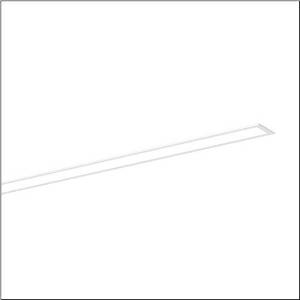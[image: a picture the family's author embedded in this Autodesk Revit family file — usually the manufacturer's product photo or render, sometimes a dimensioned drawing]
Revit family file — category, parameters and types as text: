
# Revit family: silica_21_51mx10db42wb
name_source: partatom
category: Lighting Fixtures
units: mm (PartAtom-declared; Revit-internal decimal feet)

## family parameters
Cut with Voids When Loaded = No
Host = Face
Light Source = No
Part Type = Normal
Room Calculation Point = No
Round Connector Dimension = Use Diameter
Shared = No

## types (1)
- --- (1 x LED, 3000 lm, 19 W, 4000K)
    Apparent Load = 19 VA
    CIE Flux Codes = 48 79 96 100 100
    Color Rendering = 80
    Color Temperature = 4000K
    Default Elevation = 1800 mm
    Description = Silica 21, office luminaire, primary optical cover: cover, of PMMA, opal, light emission: direct distribution, primary light characteristic: symmetric, installation type: recessed, LED, rated luminous flux: 3.000lm, luminous efficacy: 158lm/W, light colour: 840, colour temperature: 4000K, control gear: DALI 2, with terminal, 3+2-pole, max. 2.5mm², mains connection: 220..240V, AC, 50/60Hz, rated input power: 19W, luminaire housing, of aluminium, traffic white (RAL 9016), length: 1.528mm, width: 79mm, height: 53mm, protection rating (complete): IP20, insulation class (complete): insulation class I (protective earthing), certification: CE, ENEC, VDE, permissible operating ambient temperature: 0..+35°C, standard: EN 50419, packaging unit: 1 piece
    Height = 0 mm  [stored 0 ft]
    Lamp = 1 x LED
    Lamp Light Flux = 3000 lm
    Lamp Power = 19 W
    Lamp count = 1
    Length = 1527 mm
    Luminous efficacy = 158 lm/W
    Manufacturer = Siteco
    ModVariant = No
    Model = 51MX10DB42WB
    Mounting Place = Ceiling
    Mounting Type = Recessed
    Number of Poles = 1
    OnlyDefault = Yes
    Power Factor = 1
    Product Name = Silica 21
    Product group = office luminaire | ceiling recessed
    ProductGroupID = 400
    Protection Class = Protection class I
    Protection Degree = IP 20
    RLX_Detail_Level = 1
    RLX_Emergency_Light_Flux = 0 lm
    RLX_Emergency_Type = 0
    RLX_Emergency_Type_DB = No
    RlxData = <blob elided: 21033 chars, md5=160e235e>
    Socket = socket
    Standby Power = 0 W
    System Light Flux = 3000 lm
    System Power = 19 W
    Type Comments = factory setting: luminous flux: 100 % | dim-lin: 254 | 218 mA
    Type Image = l_1335891.jpg
    URL = http://relux.com
    VarID = @adj_117845
    Voltage = 0 V
    Weight = 0.00 kg
    Width = 79 mm

note: [stored X ft] marks values corroborated as IEEE doubles in the binary element streams (Revit-internal decimal feet)

## geometry (parser evidence)
native form markers: Blend x4, Sweep x9
no freeform markers — native parametric forms only
